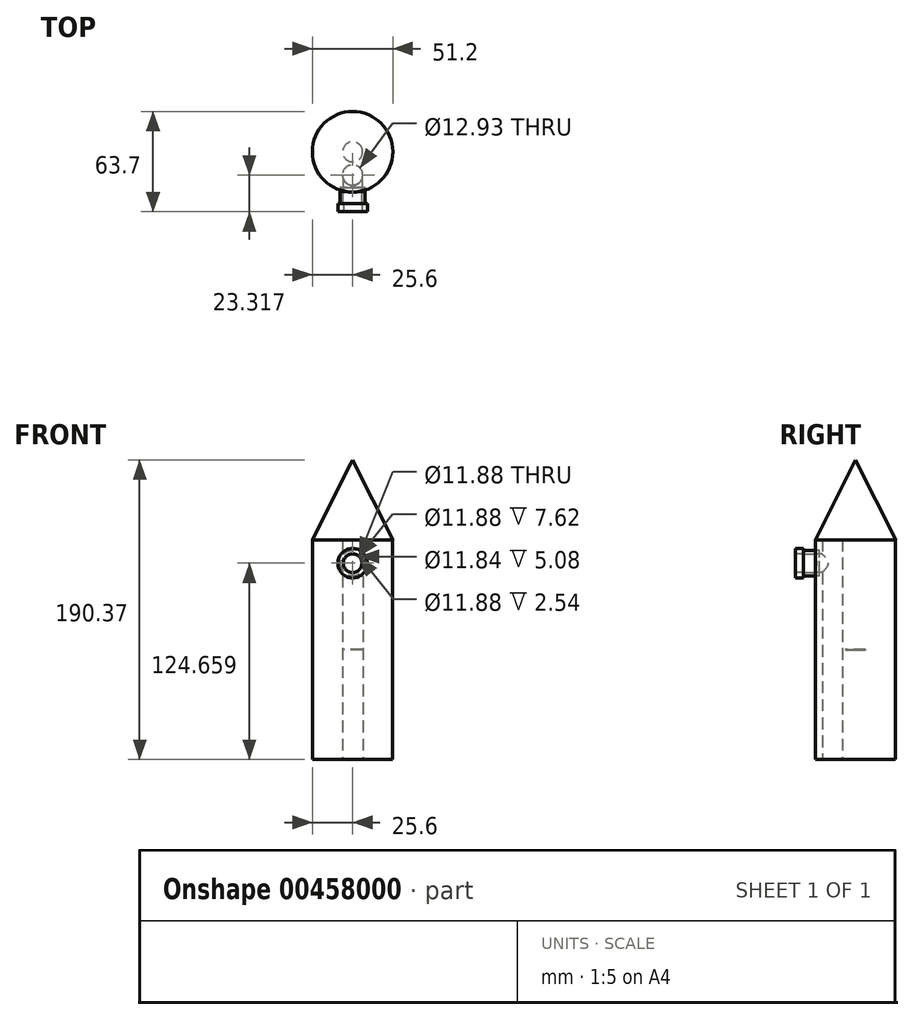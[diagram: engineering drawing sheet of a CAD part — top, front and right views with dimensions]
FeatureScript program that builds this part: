
annotation { "Feature Type Name" : "Feature", "Feature Type Description" : "" }
export const myFeature = defineFeature(function(context is Context, id is Id, definition is map)
    precondition{}
    {
        {
            var Q0;
            Q0=qCreatedBy(makeId("Top.planeOp"),FACE);
            var sketch = newSketch(context, id + "F0", { "sketchPlane" : qUnion([Q0])});
            skCircle(sketch, "E0", {"center": v(0, 0) * mm, "radius": 25.4 * mm});
            skSolve(sketch);
        }
        {
            var Q0;
            Q0=qCreatedBy(makeId("Top.planeOp"),FACE);
            var sketch = newSketch(context, id + "F1", { "sketchPlane" : qUnion([Q0])});
            skCircle(sketch, "E1", {"center": v(0, 0) * mm, "radius": 6.35 * mm});
            skSolve(sketch);
        }
        {
            var Q0;
            Q0 = qSketchRegion(id + "F1", true);
            extrude(context, id + "F2", {"entities" : qUnion([Q0]), "endBound" : BoundingType.SYMMETRIC, "depth" : 0.25 * mm});
        }
        {
            var Q0;
            Q0 = qSketchRegion(id + "F0", true);
            extrude(context, id + "F3", {"entities" : qUnion([Q0]), "endBound" : BoundingType.SYMMETRIC, "depth" : 139.7 * mm});
        }
        {
            var Q0;
            Q0=qCreatedBy(makeId("Right.planeOp"),FACE);
            var sketch = newSketch(context, id + "F4", { "sketchPlane" : qUnion([Q0])});
            skLineSegment(sketch, "E2", {"start": v(0, 88.72) * mm, "end": v(0, 139.57) * mm});
            skLineSegment(sketch, "E3", {"start": v(0, 139.57) * mm, "end": v(-25.6, 88.72) * mm});
            skLineSegment(sketch, "E4", {"start": v(-25.6, 88.72) * mm, "end": v(0, 88.72) * mm});
            skSolve(sketch);
        }
        {
            var Q0;
            Q0 = qSketchRegion(id + "F4", true);
            var Q1;
            Q1=sQuery(id+"F4.wireOp",EDGE,"E2");
            revolve(context, id + "F5", {"operationType" : NewBodyOperationType.ADD, "entities" : qUnion([Q0]), "axis" : qUnion([Q1]), "revolveType" : RevolveType.FULL});
        }
        {
            var Q0;
            Q0=makeQuery(id+"F3.opExtrude","CAP_FACE",FACE,{"disambiguationData":[OSD([sQuery(id+"F0.wireOp",EDGE,"E0")])],"isStart":true});
            var sketch = newSketch(context, id + "F6", { "sketchPlane" : qUnion([Q0])});
            skCircle(sketch, "E5", {"center": v(0, 14.78) * mm, "radius": 6.47 * mm});
            skSolve(sketch);
        }
        {
            var Q0;
            Q0 = qSketchRegion(id + "F6", true);
            extrude(context, id + "F7", {"entities" : qUnion([Q0]), "operationType" : NewBodyOperationType.REMOVE, "oppositeDirection" : true, "depth" : 152.4 * mm});
        }
        {
            var Q0;
            Q0=qCreatedBy(makeId("Front.planeOp"),FACE);
            cPlane(context, id + "F8", {"entities" : qUnion([Q0]), "cplaneType" : CPlaneType.OFFSET, "offset" : 25.4 * mm, "width" : 152.4 * mm, "height" : 152.4 * mm});
        }
        {
            var Q0;
            Q0=qCreatedBy(id+"F8.planeOp",FACE);
            var sketch = newSketch(context, id + "F9", { "sketchPlane" : qUnion([Q0])});
            skCircle(sketch, "E6", {"center": v(0, 54.8) * mm, "radius": 5.94 * mm});
            skCircle(sketch, "E7", {"center": v(0, 54.8) * mm, "radius": 7.95 * mm});
            skSolve(sketch);
        }
        {
            var Q0;
            Q0=makeQuery(id+"F9.imprint","IMPRINT",FACE,{"disambiguationData":[TD([[makeQuery(id+"F9.imprint","IMPRINT",EDGE,{"derivedFrom":sQuery(id+"F9.wireOp",EDGE,"E6")}),1.0]])]});
            extrude(context, id + "F10", {"entities" : qUnion([Q0]), "operationType" : NewBodyOperationType.REMOVE, "oppositeDirection" : true, "depth" : 12.7 * mm});
        }
        {
            var Q0;
            Q0=makeQuery(id+"F9.imprint","IMPRINT",FACE,{"disambiguationData":[TD([[makeQuery(id+"F9.imprint","IMPRINT",EDGE,{"derivedFrom":sQuery(id+"F9.wireOp",EDGE,"E6")}),-1.0]])]});
            extrude(context, id + "F11", {"entities" : qUnion([Q0]), "operationType" : NewBodyOperationType.ADD, "depth" : 12.7 * mm});
        }
        {
            var Q0;
            Q0=makeQuery(id+"F11.opExtrude","CAP_FACE",FACE,{"disambiguationData":[OSD([sQuery(id+"F9.wireOp",EDGE,"E6"),sQuery(id+"F9.wireOp",EDGE,"E7")])],"isStart":false});
            var sketch = newSketch(context, id + "F12", { "sketchPlane" : qUnion([Q0])});
            skCircle(sketch, "E8", {"center": v(0, 54.8) * mm, "radius": 9.32 * mm});
            skCircle(sketch, "E9", {"center": v(0, 54.8) * mm, "radius": 5.92 * mm});
            skSolve(sketch);
        }
        {
            var Q0;
            Q0 = qSketchRegion(id + "F12", true);
            extrude(context, id + "F13", {"entities" : qUnion([Q0]), "operationType" : NewBodyOperationType.ADD, "oppositeDirection" : true, "depth" : 5.08 * mm});
        }
        {
            var Q0;
            Q0=makeQuery(id+"F11.opExtrude","CAP_FACE",FACE,{"disambiguationData":[OSD([sQuery(id+"F9.wireOp",EDGE,"E6"),sQuery(id+"F9.wireOp",EDGE,"E7")])],"isStart":true});
            extrude(context, id + "F14", {"entities" : qUnion([Q0]), "depth" : 2.54 * mm});
        }
        {
            var Q0;
            Q0=makeQuery(id+"F5.opRevolve","SWEPT_BODY",BODY,{"disambiguationData":[OSD([sQuery(id+"F4.wireOp",EDGE,"E2"),sQuery(id+"F4.wireOp",EDGE,"E3"),sQuery(id+"F4.wireOp",EDGE,"E4")])]});
            transform(context, id + "F15", {"entities" : qUnion([Q0]), "transformType" : TransformType.TRANSLATION_3D, "dx" : 0 * mm, "dy" : 0 * mm, "dz" : -19.05 * mm, "makeCopy" : false});
        }
    });
